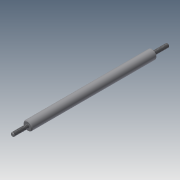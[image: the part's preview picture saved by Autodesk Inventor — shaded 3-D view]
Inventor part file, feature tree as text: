
AUTODESK INVENTOR PART (.ipt)
format: ipt  version: 2015 (Build 190159000, 159)  size: 96,256 bytes
history: native  units: mm
features: sketch x5, extrude x3, chamfer x3, hole x2, thread x2
ambient origin geometry x8: Origin, YZ Plane, XZ Plane, XY Plane, X Axis, Y Axis, Z Axis, Center Point
bodies: Solid1 (feature_tree)
feature tree (15):
  extrude  "Extrusion1"  Depth=82.6mm TaperAngle=0.0deg
  hole  "Hole1"  [1 undecoded]
  hole  "Hole2"  [1 undecoded]
  chamfer  "Chamfer1"  Distance=10.0mm
  extrude  "Extrusion2"  Depth=10.0mm TaperAngle=45.0deg
  extrude  "Extrusion3"  Depth=10.0mm TaperAngle=45.0deg
  thread  "Thread1"  [1 undecoded]
  thread  "Thread2"  [1 undecoded]
  chamfer  "Chamfer2"  [1 undecoded]
  chamfer  "Chamfer3"  [1 undecoded]
  sketch  "Sketch1"  dims[d0=6.0mm d1=82.6mm d2=0.0mm]
  sketch  "Sketch2"  dims[d3=2.459mm d4=6.0mm d5=4.0mm d6=2.0mm d7=90.0deg d8=8.0mm d9=0.0mm]
  sketch  "Sketch3"  dims[d10=2.459mm d11=6.0mm d12=4.0mm d13=2.0mm d14=90.0deg d15=8.0mm d16=0.0mm d17=0.5mm d18=2.0mm d19=45.0deg]
  sketch  "Sketch4"  dims[d20=10.0mm d21=0.0mm d22=10.0mm d23=0.0mm d24=10.0mm d25=0.0mm]
  sketch  "Sketch5"  dims[d26=10.0mm d27=0.0mm d28=0.3mm d29=2.0mm d30=45.0deg d31=0.3mm d32=2.0mm d33=45.0deg]
note: 6 required parameter values undecoded (feature->parameter linkage not recoverable at this tier; creation-order binding heuristic only, values carry confidence <= 0.55)
